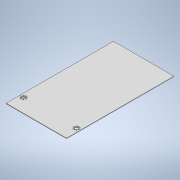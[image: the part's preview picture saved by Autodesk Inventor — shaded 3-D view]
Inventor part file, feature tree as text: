
AUTODESK INVENTOR PART (.ipt)
format: ipt  version: 2020 (Build 240168000, 168)  size: 168,448 bytes
history: native  units: in
note: dims shown in document units (in); Inventor stores cm internally (conversion verified against a paired STEP export)
features: extrude x3, sketch x3
ambient origin geometry x8: Origin, YZ Plane, XZ Plane, XY Plane, X Axis, Y Axis, Z Axis, Center Point
bodies: Solid1 (feature_tree)
feature tree (6):
  extrude  "Extrusion1"  Depth=10.0in
  extrude  "Extrusion2"  Depth=0.09in
  extrude  "Extrusion3"  Depth=0.09in
  sketch  "Sketch1"  dims[d0=10.0in d1=17.5in]
  sketch  "Sketch2"  dims[d2=0.09in d3=0.0in d5=0.5in]
  sketch  "Sketch3"  dims[d6=0.5in d23=0.1406in d24=0.1406in d25=0.1406in d26=0.1406in d27=0.1406in d28=0.1406in d29=0.1406in d30=0.1406in d31=0.5in d32=0.1406in d33=0.1406in d34=0.1406in d35=0.1406in d36=0.1406in d37=0.1406in d38=0.1406in d39=0.1406in d49=0.5in d50=0.1406in d51=0.1406in d52=0.1406in d53=0.1406in d54=0.1406in d56=0.1406in d57=0.1406in d62=0.1406in d63=0.1406in d64=0.1406in d85=0.09in d86=0.0in d148=0.2504in d149=0.0in]
